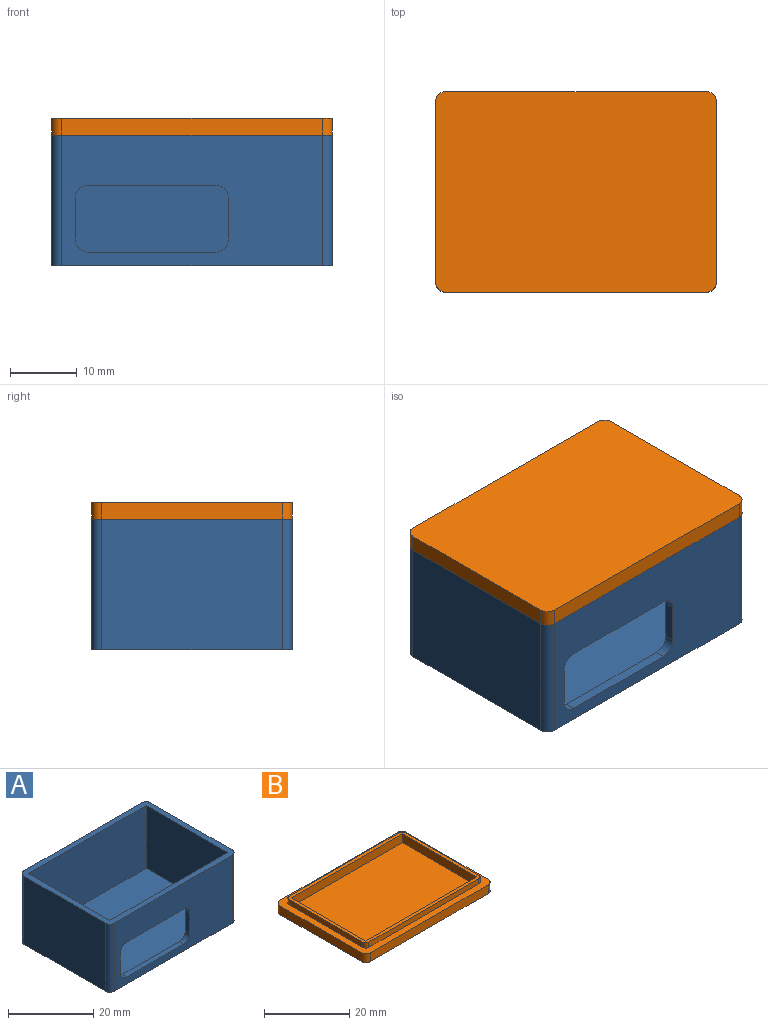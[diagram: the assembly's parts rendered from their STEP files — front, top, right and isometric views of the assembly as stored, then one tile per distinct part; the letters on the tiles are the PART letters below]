
ASSEMBLY  parts=2 mates=1
PART A: 23 faces, bbox 42x30x19.5 mm
  f0: plane 39x19.5mm, normal (0,-1,0), area 533.9mm2, adj f8,f9,f11,f14,f15,f16,f17,f18
  f1: plane 27x19.5mm, normal (1,0,0), area 526.5mm2, adj f8,f9,f11,f12
  f2: plane 39x19.5mm, normal (0,1,0), area 760.5mm2, adj f8,f9,f12,f13
  f3: plane 27x18mm, normal (-1,0,0), area 486mm2, adj f4,f6,f8,f10
  f4: plane 39x18mm, normal (0,1,0), area 475.4mm2, adj f3,f5,f8,f10,f15,f16,f17,f18
  f5: plane 27x18mm, normal (1,0,0), area 486mm2, adj f4,f6,f8,f10
  f6: plane 39x18mm, normal (0,-1,0), area 702mm2, adj f3,f5,f8,f10
  f7: plane 27x19.5mm, normal (-1,0,0), area 526.5mm2, adj f8,f9,f13,f14
  f8: plane 42x30mm, normal (0,0,1), area 205.1mm2, adj f0,f1,f2,f3,f4,f5,f6,f7
  f9: plane 42x30mm, normal (0,0,-1), area 1258.1mm2, adj f0,f1,f2,f7,f11,f12,f13,f14
  f10: plane 39x27mm, normal (0,0,1), area 1053mm2, adj f3,f4,f5,f6
  f11: cylinder r=1.5mm len=19.5mm, axis (0,0,1), area 45.9mm2, adj f0,f1,f8,f9
  f12: cylinder r=1.5mm len=19.5mm, axis (0,0,-1), area 45.9mm2, adj f1,f2,f8,f9
  f13: cylinder r=1.5mm len=19.5mm, axis (0,0,1), area 45.9mm2, adj f2,f7,f8,f9
  f14: cylinder r=1.5mm len=19.5mm, axis (0,0,-1), area 45.9mm2, adj f0,f7,f8,f9
  f15: plane 19x1.5mm, normal (0,0,1), area 28.5mm2, adj f0,f4,f19,f20
  f16: plane 6x1.5mm, normal (1,0,0), area 9mm2, adj f0,f4,f19,f21
  f17: plane 6x1.5mm, normal (-1,0,0), area 9mm2, adj f0,f4,f20,f22
  f18: plane 19x1.5mm, normal (0,0,-1), area 28.5mm2, adj f0,f4,f21,f22
  f19: cylinder r=2mm len=2mm, axis (0,-1,0), area 4.7mm2, adj f0,f4,f15,f16
  f20: cylinder r=2mm len=2mm, axis (0,1,0), area 4.7mm2, adj f0,f4,f15,f17
  f21: cylinder r=2mm len=2mm, axis (0,1,0), area 4.7mm2, adj f0,f4,f16,f18
  f22: cylinder r=2mm len=2mm, axis (0,-1,0), area 4.7mm2, adj f0,f4,f17,f18
PART B: 24 faces, bbox 42x30x4 mm
  f0: plane 42x30mm, normal (0,0,1), area 245.2mm2, adj f1,f2,f3,f4,f5,f6,f7,f12
  f1: plane 39x2.5mm, normal (0,-1,0), area 97.5mm2, adj f0,f14,f17,f22
  f2: plane 27x2.5mm, normal (1,0,0), area 67.5mm2, adj f0,f14,f15,f22
  f3: plane 39x2.5mm, normal (0,1,0), area 97.5mm2, adj f0,f15,f16,f22
  f4: plane 27x2.5mm, normal (-1,0,0), area 67.5mm2, adj f0,f16,f17,f22
  f5: plane 36.4x1.5mm, normal (0,-1,0), area 54.6mm2, adj f0,f13,f18,f21
  f6: plane 24.4x1.5mm, normal (1,0,0), area 36.6mm2, adj f0,f13,f18,f19
  f7: plane 36.4x1.5mm, normal (0,1,0), area 54.6mm2, adj f0,f13,f19,f20
  f8: plane 24.8x2.5mm, normal (-1,0,0), area 62mm2, adj f9,f11,f13,f23
  f9: plane 36.8x2.5mm, normal (0,1,0), area 92mm2, adj f8,f10,f13,f23
  f10: plane 24.8x2.5mm, normal (1,0,0), area 62mm2, adj f9,f11,f13,f23
  f11: plane 36.8x2.5mm, normal (0,-1,0), area 92mm2, adj f8,f10,f13,f23
  f12: plane 24.4x1.5mm, normal (-1,0,0), area 36.6mm2, adj f0,f13,f20,f21
  f13: plane 38.4x26.4mm, normal (0,0,1), area 100.3mm2, adj f5,f6,f7,f8,f9,f10,f11,f12
  f14: cylinder r=1.5mm len=2.5mm, axis (0,0,-1), area 5.9mm2, adj f0,f1,f2,f22
  f15: cylinder r=1.5mm len=2.5mm, axis (0,0,1), area 5.9mm2, adj f0,f2,f3,f22
  f16: cylinder r=1.5mm len=2.5mm, axis (0,0,-1), area 5.9mm2, adj f0,f3,f4,f22
  f17: cylinder r=1.5mm len=2.5mm, axis (0,0,1), area 5.9mm2, adj f0,f1,f4,f22
  f18: cylinder r=1mm len=1.5mm, axis (0,0,1), area 2.4mm2, adj f0,f5,f6,f13
  f19: cylinder r=1mm len=1.5mm, axis (0,0,-1), area 2.4mm2, adj f0,f6,f7,f13
  f20: cylinder r=1mm len=1.5mm, axis (0,0,1), area 2.4mm2, adj f0,f7,f12,f13
  f21: cylinder r=1mm len=1.5mm, axis (0,0,-1), area 2.4mm2, adj f0,f5,f12,f13
  f22: plane 42x30mm, normal (0,0,-1), area 1258.1mm2, adj f1,f2,f3,f4,f14,f15,f16,f17
  f23: plane 36.8x24.8mm, normal (0,0,1), area 912.6mm2, adj f8,f9,f10,f11
PLACE A t=(-4.29,4.2,0.27)mm
PLACE B rot(axis=(1,0,0),180deg) t=(-4.29,4.2,19.77)mm
MATE fastened B.f17 <-> A.f13  axis (0,0,-1) through (-23.79,17.7,19.77)mm
